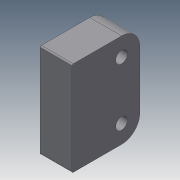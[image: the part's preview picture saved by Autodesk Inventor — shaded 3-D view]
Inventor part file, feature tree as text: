
AUTODESK INVENTOR PART (.ipt)
format: ipt  version: 2020.3 (Build 243373000, 373)  size: 103,936 bytes
history: native  units: in
note: dims shown in document units (in); Inventor stores cm internally (conversion verified against a paired STEP export)
features: extrude x1, sketch x1
ambient origin geometry x8: Origin, YZ Plane, XZ Plane, XY Plane, X Axis, Y Axis, Z Axis, Center Point
bodies: Solid1 (feature_tree)
feature tree (2):
  extrude  "Extrusion1"  [1 undecoded]
  sketch  "Sketch1"  dims[d0=0.48in d1=0.0in]
note: 1 required parameter value undecoded (feature->parameter linkage not recoverable at this tier; creation-order binding heuristic only, values carry confidence <= 0.55)
